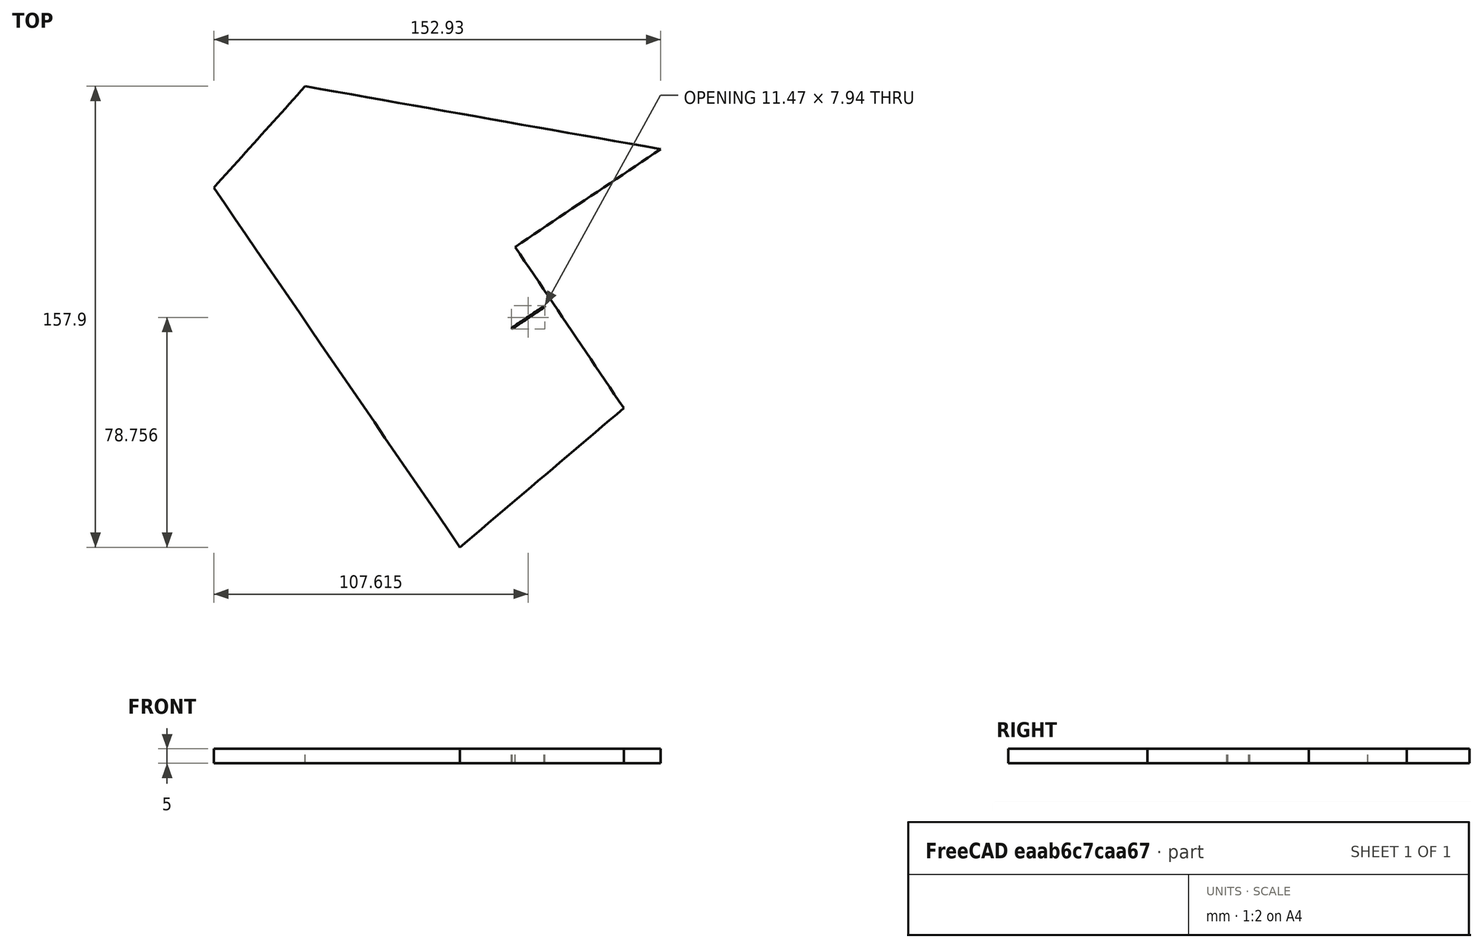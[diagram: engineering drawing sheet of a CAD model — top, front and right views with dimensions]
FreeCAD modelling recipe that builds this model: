
FCSTD DOCUMENT  (FreeCAD 0.19R)
Label: F-35_v2_parts_16
License: All rights reserved
LicenseURL: http://en.wikipedia.org/wiki/All_rights_reserved
objects: App::DocumentObjectGroup×2, PartDesign::CoordinateSystem×2, App::FeaturePython×1, Sketcher::SketchObject×1, PartDesign::Pad×1, PartDesign::Body×1, App::Part×1
note: 6 computed .brp shape members not serialized (recipe doc carries the construction recipe); baked Part::Feature solids carry a one-line shape summary decoded from their .brp

FEATURE [App::DocumentObjectGroup] Parts
FEATURE [PartDesign::CoordinateSystem] LCS_Origin
  AttacherType = Attacher::AttachEngine3D
  MapMode = 2
  Support = -> [X_Axis]
FEATURE [App::DocumentObjectGroup] Constraints
FEATURE [App::FeaturePython] Variables  # WARN: FeaturePython — macro-defined, semantics opaque (R4)
FEATURE [Sketcher::SketchObject] Sketch003
  FullyConstrained = false
  sketch-geometry (10):
    g0: BSplineCurve PolesCount=2 KnotsCount=2 Degree=1 IsPeriodic=0
    g1: BSplineCurve PolesCount=2 KnotsCount=2 Degree=1 IsPeriodic=0
    g2: BSplineCurve PolesCount=2 KnotsCount=2 Degree=1 IsPeriodic=0
    g3: BSplineCurve PolesCount=2 KnotsCount=2 Degree=1 IsPeriodic=0
    g4: BSplineCurve PolesCount=2 KnotsCount=2 Degree=1 IsPeriodic=0
    g5: BSplineCurve PolesCount=2 KnotsCount=2 Degree=1 IsPeriodic=0
    g6: BSplineCurve PolesCount=2 KnotsCount=2 Degree=1 IsPeriodic=0
    g7: BSplineCurve PolesCount=2 KnotsCount=2 Degree=1 IsPeriodic=0
    g8: BSplineCurve PolesCount=2 KnotsCount=2 Degree=1 IsPeriodic=0
    g9: BSplineCurve PolesCount=2 KnotsCount=2 Degree=1 IsPeriodic=0
FEATURE [PartDesign::Pad] Pad003
  Direction = (1,1,1)
  Length = 5
  Length2 = 100
  Profile = -> Sketch003
  Type = 0
FEATURE [PartDesign::Body] Body003  label="Part16"
  Group = -> [Sketch003,Pad003]
  Origin = -> Origin004
  Tip = -> Pad003
FEATURE [PartDesign::CoordinateSystem] LCS_1
  AttacherType = Attacher::AttachEngine3D
  MapMode = 7
  Placement = pos=(313.713,-196.302,5) rot=(-0.211048,0.69118,0.69118;3.55758rad)
  Support = -> [Pad003]
FEATURE [App::Part] Model
  Configuration = 0
  Group = -> [LCS_Origin,Constraints,Variables,Body003,LCS_1]
  Origin = -> Origin
  Type = Assembly4 Model
